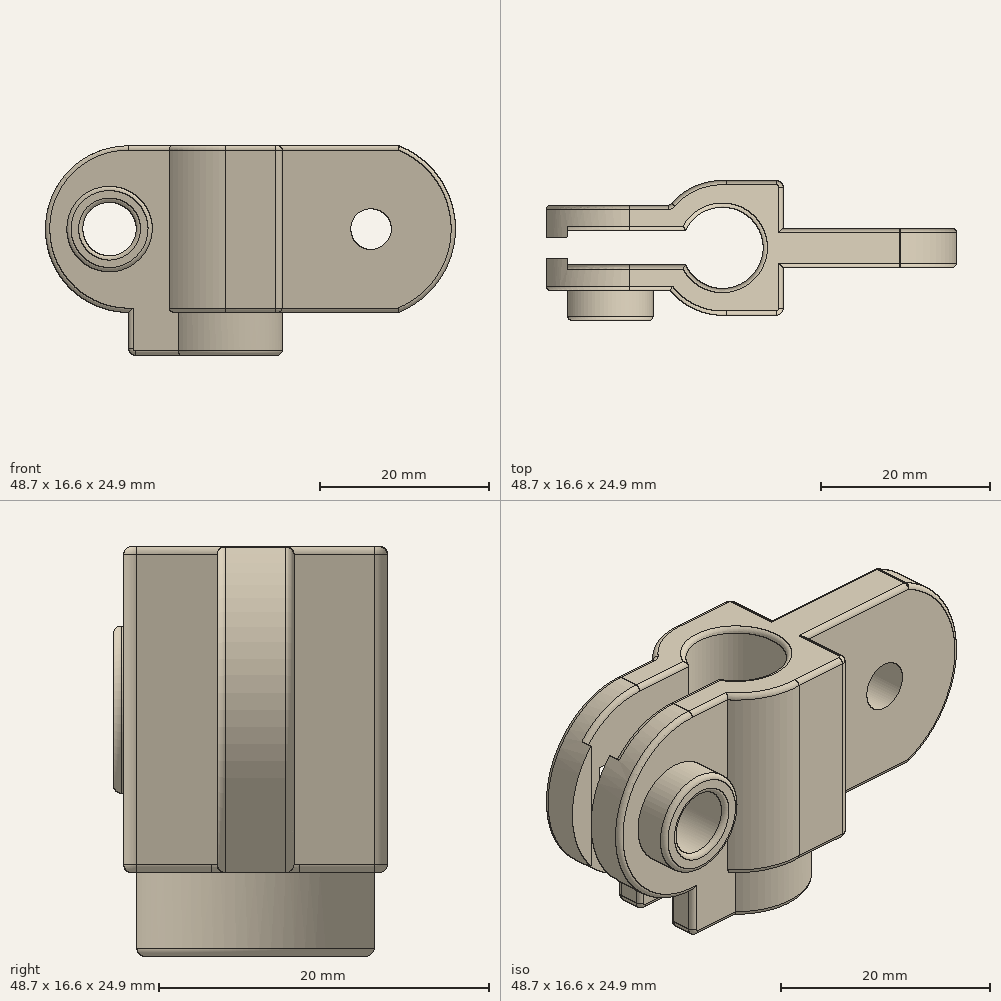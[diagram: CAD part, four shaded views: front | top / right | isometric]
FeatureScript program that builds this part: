
annotation { "Feature Type Name" : "Feature", "Feature Type Description" : "" }
export const myFeature = defineFeature(function(context is Context, id is Id, definition is map)
    precondition{}
    {
        {
            var Q0;
            Q0=qCreatedBy(makeId("Front.planeOp"),FACE);
            var sketch = newSketch(context, id + "F0", { "sketchPlane" : qUnion([Q0])});
            skLineSegment(sketch, "E0.bottom", {"start": v(4.6, 9.9) * mm, "end": v(-11.3, 9.9) * mm});
            skLineSegment(sketch, "E0.top", {"start": v(4.6, -9.9) * mm, "end": v(-11.3, -9.9) * mm});
            skLineSegment(sketch, "E0.right", {"start": v(-11.3, 9.9) * mm, "end": v(-11.3, -9.9) * mm});
            skPoint(sketch, "E0.middle", {"position": v(0, 0) * mm});
            skPoint(sketch, "E1.orphan", {"position": v(11.3, -9.9) * mm});
            skPoint(sketch, "E2.orphan", {"position": v(11.3, 9.9) * mm});
            skPoint(sketch, "E3.start.orphan", {"position": v(11.3, 0) * mm});
            skArc(sketch, "E4.trimOffspring", {"start": v(4.6, -9.9) * mm, "mid": v(11.3, 0) * mm, "end": v(4.6, 9.9) * mm});
            skLineSegment(sketch, "E5", {"start": v(11.3, 0) * mm, "end": v(3.68, 0) * mm});
            skLineSegment(sketch, "E6", {"start": v(-11.3, -9.9) * mm, "end": v(-9.3, -9.9) * mm});
            skLineSegment(sketch, "E7", {"start": v(-9.3, -9.9) * mm, "end": v(-9.3, 9.9) * mm});
            skPoint(sketch, "E8.endSnap0", {"position": v(-9.3, 0) * mm});
            skLineSegment(sketch, "E9", {"start": v(3.68, 0) * mm, "end": v(-1.14, 0) * mm});
            skCircle(sketch, "E10", {"center": v(1.27, 0) * mm, "radius": 2.41 * mm});
            skSolve(sketch);
        }
        {
            var Q0;
            Q0 = qSketchRegion(id + "F0", true);
            extrude(context, id + "F1", {"entities" : qUnion([Q0]), "depth" : 4.67 * mm});
        }
        {
            var Q0;
            Q0=makeQuery(id+"F1.opExtrude","SWEPT_FACE",FACE,{"disambiguationData":[OSD([sQuery(id+"F0.wireOp",EDGE,"E0.bottom")])]});
            var sketch = newSketch(context, id + "F2", { "sketchPlane" : qUnion([Q0])});
            skLineSegment(sketch, "E11", {"start": v(-11.3, -4.67) * mm, "end": v(-9.3, -4.67) * mm});
            skLineSegment(sketch, "E12", {"start": v(-9.3, -4.67) * mm, "end": v(-9.3, 0) * mm});
            skLineSegment(sketch, "E13", {"start": v(-9.3, 0) * mm, "end": v(-11.3, 0) * mm});
            skPoint(sketch, "E14.endSnap0", {"position": v(-11.3, -2.34) * mm});
            skLineSegment(sketch, "E15", {"start": v(-9.3, -2.34) * mm, "end": v(-9.3, -10.34) * mm});
            skLineSegment(sketch, "E16", {"start": v(-9.3, -9.55) * mm, "end": v(-9.3, 4.88) * mm});
            skLineSegment(sketch, "E17", {"start": v(-10.08, 5.66) * mm, "end": v(-17, 5.66) * mm});
            skLineSegment(sketch, "E18", {"start": v(-10.08, -10.34) * mm, "end": v(-17, -10.34) * mm});
            skLineSegment(sketch, "E19", {"start": v(-22.7, -7.42) * mm, "end": v(-27.19, -7.42) * mm});
            skLineSegment(sketch, "E20", {"start": v(-22.7, 2.74) * mm, "end": v(-26.33, 2.74) * mm});
            skArc(sketch, "E21", {"start": v(-16, 5.66) * mm, "mid": v(-19.7, 5.01) * mm, "end": v(-22.7, 2.74) * mm});
            skPoint(sketch, "E21.third.point", {"position": v(-16, 5.66) * mm});
            skPoint(sketch, "E22.orphan", {"position": v(-22.7, 5.66) * mm});
            skPoint(sketch, "E23.orphan", {"position": v(-22.7, -10.34) * mm});
            skArc(sketch, "E24.trimOffspring", {"start": v(-22.7, -7.42) * mm, "mid": v(-19.7, -9.69) * mm, "end": v(-16, -10.34) * mm});
            skArc(sketch, "E25", {"start": v(-20.88, -4.37) * mm, "mid": v(-11.68, -2.34) * mm, "end": v(-20.88, -0.3) * mm});
            skLineSegment(sketch, "E26", {"start": v(-22.7, -0.3) * mm, "end": v(-20.88, -0.3) * mm});
            skLineSegment(sketch, "E27", {"start": v(-22.7, -4.37) * mm, "end": v(-20.88, -4.37) * mm});
            skPoint(sketch, "E28.visualSharp", {"position": v(-9.3, -10.34) * mm});
            skArc(sketch, "E28.filletArc", {"start": v(-10.08, -10.34) * mm, "mid": v(-9.53, -10.1) * mm, "end": v(-9.3, -9.55) * mm});
            skPoint(sketch, "E29.visualSharp", {"position": v(-9.3, 5.66) * mm});
            skArc(sketch, "E29.filletArc", {"start": v(-9.3, 4.88) * mm, "mid": v(-9.53, 5.43) * mm, "end": v(-10.08, 5.66) * mm});
            skLineSegment(sketch, "E30", {"start": v(-20.88, -0.3) * mm, "end": v(-35.62, -0.3) * mm});
            skLineSegment(sketch, "E31", {"start": v(-35.62, 2.74) * mm, "end": v(-22.7, 2.74) * mm});
            skLineSegment(sketch, "E32", {"start": v(-22.7, -4.37) * mm, "end": v(-35.62, -4.37) * mm});
            skLineSegment(sketch, "E33", {"start": v(-35.62, -7.42) * mm, "end": v(-27.19, -7.42) * mm});
            skLineSegment(sketch, "E34", {"start": v(-22.7, 2.74) * mm, "end": v(-31.35, 2.74) * mm});
            skLineSegment(sketch, "E35", {"start": v(-22.7, 2.74) * mm, "end": v(-37.44, 2.74) * mm});
            skLineSegment(sketch, "E36", {"start": v(-35.62, -0.3) * mm, "end": v(-37.44, -0.3) * mm});
            skLineSegment(sketch, "E37", {"start": v(-37.44, -0.3) * mm, "end": v(-37.44, 2.74) * mm});
            skLineSegment(sketch, "E38", {"start": v(-37.44, -4.37) * mm, "end": v(-37.44, -7.42) * mm});
            skLineSegment(sketch, "E39", {"start": v(-37.44, -7.42) * mm, "end": v(-35.62, -7.42) * mm});
            skLineSegment(sketch, "E40", {"start": v(-35.62, -4.37) * mm, "end": v(-37.44, -4.37) * mm});
            skSolve(sketch);
        }
        {
            var Q0;
            Q0 = qSketchRegion(id + "F2", true);
            extrude(context, id + "F3", {"entities" : qUnion([Q0]), "operationType" : NewBodyOperationType.ADD, "oppositeDirection" : true, "depth" : 19.8 * mm});
        }
        {
            var Q0;
            Q0=makeQuery(id+"F3.opExtrude","CAP_EDGE",EDGE,{"disambiguationData":[OSD([sQuery(id+"F2.wireOp",EDGE,"E37")])],"isStart":true});
            var Q1;
            Q1=makeQuery(id+"F3.opExtrude","CAP_EDGE",EDGE,{"disambiguationData":[OSD([sQuery(id+"F2.wireOp",EDGE,"E38")])],"isStart":true});
            var Q2;
            Q2=makeQuery(id+"F3.opExtrude","CAP_EDGE",EDGE,{"disambiguationData":[OSD([sQuery(id+"F2.wireOp",EDGE,"E37")])],"isStart":false});
            var Q3;
            Q3=makeQuery(id+"F3.opExtrude","CAP_EDGE",EDGE,{"disambiguationData":[OSD([sQuery(id+"F2.wireOp",EDGE,"E38")])],"isStart":false});
            fillet(context, id + "F4", {"entities" : qUnion([Q0, Q1, Q2, Q3]), "radius" : 9.9 * mm, "tangentPropagation" : true, "allowEdgeOverflow" : false});
        }
        {
            var Q0;
            Q0=makeQuery(id+"F3.opExtrude","SWEPT_FACE",FACE,{"disambiguationData":[OSD([sQuery(id+"F2.wireOp",EDGE,"E35")])]});
            var sketch = newSketch(context, id + "F5", { "sketchPlane" : qUnion([Q0])});
            skPoint(sketch, "E41.endSnap0", {"position": v(35.62, 0) * mm});
            skLineSegment(sketch, "E42", {"start": v(26.64, 0) * mm, "end": v(22.7, 0) * mm});
            skLineSegment(sketch, "E43", {"start": v(33, 0) * mm, "end": v(37.44, 0) * mm});
            skLineSegment(sketch, "E44", {"start": v(29.82, 3.17) * mm, "end": v(26.64, 3.18) * mm});
            skLineSegment(sketch, "E45", {"start": v(26.64, 3.18) * mm, "end": v(26.64, -3.17) * mm});
            skLineSegment(sketch, "E46", {"start": v(26.64, -3.17) * mm, "end": v(33, -3.17) * mm});
            skLineSegment(sketch, "E47", {"start": v(33, -3.17) * mm, "end": v(33, 3.17) * mm});
            skLineSegment(sketch, "E48", {"start": v(33, 3.17) * mm, "end": v(29.82, 3.17) * mm});
            skSolve(sketch);
        }
        {
            var Q0;
            Q0 = qSketchRegion(id + "F5", true);
            extrude(context, id + "F6", {"entities" : qUnion([Q0]), "operationType" : NewBodyOperationType.REMOVE, "oppositeDirection" : true, "depth" : 5.08 * mm});
        }
        {
            var Q0;
            Q0=makeQuery(id+"F3.opExtrude","SWEPT_FACE",FACE,{"disambiguationData":[OSD([sQuery(id+"F2.wireOp",EDGE,"E27"),sQuery(id+"F2.wireOp",EDGE,"E32"),sQuery(id+"F2.wireOp",EDGE,"E40")])]});
            var sketch = newSketch(context, id + "F7", { "sketchPlane" : qUnion([Q0])});
            skLineSegment(sketch, "E49", {"start": v(26.64, 0) * mm, "end": v(22.7, 0) * mm});
            skLineSegment(sketch, "E50", {"start": v(33, 0) * mm, "end": v(37.44, 0) * mm});
            skCircle(sketch, "E51", {"center": v(29.82, 0) * mm, "radius": 3.18 * mm});
            skSolve(sketch);
        }
        {
            var Q0;
            Q0 = qSketchRegion(id + "F7", true);
            extrude(context, id + "F8", {"entities" : qUnion([Q0]), "operationType" : NewBodyOperationType.REMOVE, "oppositeDirection" : true, "depth" : 25.4 * mm});
        }
        {
            var Q0;
            Q0=makeQuery(id+"F3.boolean.opBoolean","MERGE",FACE,{"derivedFrom":[makeQuery(id+"F1.opExtrude","SWEPT_FACE",FACE,{"disambiguationData":[OSD([sQuery(id+"F0.wireOp",EDGE,"E0.top"),sQuery(id+"F0.wireOp",EDGE,"E6")])]}),makeQuery(id+"F3.opExtrude","CAP_FACE",FACE,{"disambiguationData":[OSD([sQuery(id+"F2.wireOp",EDGE,"E16"),sQuery(id+"F2.wireOp",EDGE,"E17"),sQuery(id+"F2.wireOp",EDGE,"E18"),sQuery(id+"F2.wireOp",EDGE,"E19"),sQuery(id+"F2.wireOp",EDGE,"E21"),sQuery(id+"F2.wireOp",EDGE,"E24.trimOffspring"),sQuery(id+"F2.wireOp",EDGE,"E25"),sQuery(id+"F2.wireOp",EDGE,"E27"),sQuery(id+"F2.wireOp",EDGE,"E28.filletArc"),sQuery(id+"F2.wireOp",EDGE,"E29.filletArc"),sQuery(id+"F2.wireOp",EDGE,"E30"),sQuery(id+"F2.wireOp",EDGE,"E32"),sQuery(id+"F2.wireOp",EDGE,"E33"),sQuery(id+"F2.wireOp",EDGE,"E35"),sQuery(id+"F2.wireOp",EDGE,"E36"),sQuery(id+"F2.wireOp",EDGE,"E37"),sQuery(id+"F2.wireOp",EDGE,"E38"),sQuery(id+"F2.wireOp",EDGE,"E39"),sQuery(id+"F2.wireOp",EDGE,"E40")])],"isStart":false})]});
            var sketch = newSketch(context, id + "F9", { "sketchPlane" : qUnion([Q0])});
            skArc(sketch, "E52", {"start": v(-20.88, 0.3) * mm, "mid": v(-11.68, 2.34) * mm, "end": v(-20.88, 4.37) * mm});
            skArc(sketch, "E53", {"start": v(-21.62, -2.74) * mm, "mid": v(-9.3, 2.34) * mm, "end": v(-21.62, 7.42) * mm});
            skLineSegment(sketch, "E54", {"start": v(-22.7, -2.74) * mm, "end": v(-21.62, -2.74) * mm});
            skLineSegment(sketch, "E55", {"start": v(-1.45, 7.42) * mm, "end": v(-1.45, 7.82) * mm});
            skLineSegment(sketch, "E56", {"start": v(-20.88, 4.37) * mm, "end": v(-27.53, 4.37) * mm});
            skLineSegment(sketch, "E57", {"start": v(-21.62, 7.42) * mm, "end": v(-27.53, 7.42) * mm});
            skLineSegment(sketch, "E58", {"start": v(-27.53, 7.42) * mm, "end": v(-27.53, 4.37) * mm});
            skLineSegment(sketch, "E59", {"start": v(-22.7, -2.74) * mm, "end": v(-27.53, -2.74) * mm});
            skLineSegment(sketch, "E60", {"start": v(-27.53, -2.74) * mm, "end": v(-27.53, 0.3) * mm});
            skLineSegment(sketch, "E61", {"start": v(-27.53, 0.3) * mm, "end": v(-20.88, 0.3) * mm});
            skSolve(sketch);
        }
        {
            var Q0;
            Q0 = qSketchRegion(id + "F9", true);
            extrude(context, id + "F10", {"entities" : qUnion([Q0]), "operationType" : NewBodyOperationType.ADD, "depth" : 5.08 * mm});
        }
        {
            var Q0;
            Q0=makeQuery(id+"F10.opExtrude","CAP_EDGE",EDGE,{"disambiguationData":[OSD([sQuery(id+"F9.wireOp",EDGE,"E58")])],"isStart":false});
            var Q1;
            Q1=makeQuery(id+"F10.opExtrude","CAP_EDGE",EDGE,{"disambiguationData":[OSD([sQuery(id+"F9.wireOp",EDGE,"E60")])],"isStart":false});
            fillet(context, id + "F11", {"entities" : qUnion([Q0, Q1]), "radius" : 0.79 * mm, "tangentPropagation" : true, "allowEdgeOverflow" : false});
        }
        {
            var Q0;
            Q0=makeQuery(id+"F3.opExtrude","CAP_EDGE",EDGE,{"disambiguationData":[OSD([sQuery(id+"F2.wireOp",EDGE,"E21")])],"isStart":false});
            var Q1;
            {var subQ0=sQuery(id+"F2.wireOp",EDGE,"E29.filletArc");var subQ1=sQuery(id+"F2.wireOp",EDGE,"E16");Q1=makeQuery(id+"F3.boolean.opBoolean","SPLIT",EDGE,{"disambiguationData":[TD([makeQuery(id+"F3.opExtrude","SWEPT_FACE",FACE,{"disambiguationData":[OSD([subQ0])]})])],"derivedFrom":makeQuery(id+"F3.opExtrude","CAP_EDGE",EDGE,{"disambiguationData":[OSD([subQ1])],"isStart":false})});}
            var Q2;
            Q2=makeQuery(id+"F1.opExtrude","CAP_EDGE",EDGE,{"disambiguationData":[OSD([sQuery(id+"F0.wireOp",EDGE,"E0.top"),sQuery(id+"F0.wireOp",EDGE,"E6")])],"isStart":true});
            var Q3;
            Q3=makeQuery(id+"F1.opExtrude","CAP_EDGE",EDGE,{"disambiguationData":[OSD([sQuery(id+"F0.wireOp",EDGE,"E0.top"),sQuery(id+"F0.wireOp",EDGE,"E6")])],"isStart":false});
            var Q4;
            Q4=makeQuery(id+"F1.opExtrude","CAP_EDGE",EDGE,{"disambiguationData":[OSD([sQuery(id+"F0.wireOp",EDGE,"E4.trimOffspring")])],"isStart":false});
            var Q5;
            Q5=makeQuery(id+"F1.opExtrude","CAP_EDGE",EDGE,{"disambiguationData":[OSD([sQuery(id+"F0.wireOp",EDGE,"E4.trimOffspring")])],"isStart":true});
            var Q6;
            {var subQ0=sQuery(id+"F2.wireOp",EDGE,"E28.filletArc");var subQ1=sQuery(id+"F2.wireOp",EDGE,"E16");Q6=makeQuery(id+"F3.boolean.opBoolean","SPLIT",EDGE,{"disambiguationData":[TD([makeQuery(id+"F3.opExtrude","SWEPT_FACE",FACE,{"disambiguationData":[OSD([subQ0])]})])],"derivedFrom":makeQuery(id+"F3.opExtrude","CAP_EDGE",EDGE,{"disambiguationData":[OSD([subQ1])],"isStart":false})});}
            var Q7;
            Q7=makeQuery(id+"F3.opExtrude","CAP_EDGE",EDGE,{"disambiguationData":[OSD([sQuery(id+"F2.wireOp",EDGE,"E24.trimOffspring")])],"isStart":false});
            var Q8;
            Q8=makeQuery(id+"F10.opExtrude","CAP_FACE",FACE,{"disambiguationData":[OSD([sQuery(id+"F9.wireOp",EDGE,"E52"),sQuery(id+"F9.wireOp",EDGE,"E53"),sQuery(id+"F9.wireOp",EDGE,"E54"),sQuery(id+"F9.wireOp",EDGE,"E56"),sQuery(id+"F9.wireOp",EDGE,"E57"),sQuery(id+"F9.wireOp",EDGE,"E58"),sQuery(id+"F9.wireOp",EDGE,"E59"),sQuery(id+"F9.wireOp",EDGE,"E60"),sQuery(id+"F9.wireOp",EDGE,"E61")])],"isStart":false});
            fillet(context, id + "F12", {"entities" : qUnion([Q0, Q1, Q2, Q3, Q4, Q5, Q6, Q7, Q8]), "radius" : 0.5 * mm, "tangentPropagation" : true, "allowEdgeOverflow" : false});
        }
        {
            var Q0;
            Q0=makeQuery(id+"F10.boolean.opBoolean","MERGE",FACE,{"derivedFrom":[makeQuery(id+"F3.opExtrude","SWEPT_FACE",FACE,{"disambiguationData":[OSD([sQuery(id+"F2.wireOp",EDGE,"E19"),sQuery(id+"F2.wireOp",EDGE,"E33"),sQuery(id+"F2.wireOp",EDGE,"E39")])]}),makeQuery(id+"F10.opExtrude","SWEPT_FACE",FACE,{"disambiguationData":[OSD([sQuery(id+"F9.wireOp",EDGE,"E57")])]})]});
            var sketch = newSketch(context, id + "F13", { "sketchPlane" : qUnion([Q0])});
            skCircle(sketch, "E62", {"center": v(-29.82, 0) * mm, "radius": 3.18 * mm});
            skLineSegment(sketch, "E63", {"start": v(-26.64, 0) * mm, "end": v(-24.74, 0) * mm});
            skCircle(sketch, "E64", {"center": v(-29.82, 0) * mm, "radius": 5.08 * mm});
            skLineSegment(sketch, "E65", {"start": v(-33, 0) * mm, "end": v(-34.9, 0) * mm});
            skSolve(sketch);
        }
        {
            var Q0;
            Q0 = qSketchRegion(id + "F13", true);
            extrude(context, id + "F14", {"entities" : qUnion([Q0]), "operationType" : NewBodyOperationType.ADD, "depth" : 3.56 * mm});
        }
        {
            var Q0;
            Q0=makeQuery(id+"F14.opExtrude","CAP_FACE",FACE,{"disambiguationData":[OSD([sQuery(id+"F13.wireOp",EDGE,"E62"),sQuery(id+"F13.wireOp",EDGE,"E64")])],"isStart":false});
            var Q1;
            Q1=makeQuery(id+"F10.boolean.opBoolean","MERGE",FACE,{"derivedFrom":[makeQuery(id+"F3.opExtrude","SWEPT_FACE",FACE,{"disambiguationData":[OSD([sQuery(id+"F2.wireOp",EDGE,"E35")])]}),makeQuery(id+"F10.opExtrude","SWEPT_FACE",FACE,{"disambiguationData":[OSD([sQuery(id+"F9.wireOp",EDGE,"E54"),sQuery(id+"F9.wireOp",EDGE,"E59")])]})]});
            fillet(context, id + "F15", {"entities" : qUnion([Q0, Q1]), "radius" : 0.5 * mm, "tangentPropagation" : true, "allowEdgeOverflow" : false});
        }
        {
            var Q0;
            Q0=makeQuery(id+"F10.boolean.opBoolean","MERGE",FACE,{"derivedFrom":[makeQuery(id+"F3.opExtrude","SWEPT_FACE",FACE,{"disambiguationData":[OSD([sQuery(id+"F2.wireOp",EDGE,"E30"),sQuery(id+"F2.wireOp",EDGE,"E36")])]}),makeQuery(id+"F10.opExtrude","SWEPT_FACE",FACE,{"disambiguationData":[OSD([sQuery(id+"F9.wireOp",EDGE,"E61")])]})]});
            var sketch = newSketch(context, id + "F16", { "sketchPlane" : qUnion([Q0])});
            skLineSegment(sketch, "E66", {"start": v(-34.9, -0.25) * mm, "end": v(-34.9, 6.63) * mm});
            skLineSegment(sketch, "E67", {"start": v(-34.9, -0.25) * mm, "end": v(-34.9, -6.63) * mm});
            skArc(sketch, "E68", {"start": v(-34.9, 6.63) * mm, "mid": v(-37.44, 0) * mm, "end": v(-34.9, -6.63) * mm});
            skPoint(sketch, "E69.start.orphan", {"position": v(-37.44, -0.25) * mm});
            skSolve(sketch);
        }
        {
            var Q0;
            Q0 = qSketchRegion(id + "F16", true);
            extrude(context, id + "F17", {"entities" : qUnion([Q0]), "operationType" : NewBodyOperationType.ADD, "depth" : 0.76 * mm});
        }
        {
            var Q0;
            Q0=makeQuery(id+"F10.boolean.opBoolean","MERGE",FACE,{"derivedFrom":[makeQuery(id+"F3.opExtrude","SWEPT_FACE",FACE,{"disambiguationData":[OSD([sQuery(id+"F2.wireOp",EDGE,"E27"),sQuery(id+"F2.wireOp",EDGE,"E32"),sQuery(id+"F2.wireOp",EDGE,"E40")])]}),makeQuery(id+"F10.opExtrude","SWEPT_FACE",FACE,{"disambiguationData":[OSD([sQuery(id+"F9.wireOp",EDGE,"E56")])]})]});
            var sketch = newSketch(context, id + "F18", { "sketchPlane" : qUnion([Q0])});
            skLineSegment(sketch, "E70", {"start": v(34.9, 6.62) * mm, "end": v(34.9, -6.62) * mm});
            skArc(sketch, "E71", {"start": v(34.9, -6.62) * mm, "mid": v(37.44, 0) * mm, "end": v(34.9, 6.62) * mm});
            skPoint(sketch, "E72.start.orphan", {"position": v(37.44, 0) * mm});
            skSolve(sketch);
        }
        {
            var Q0;
            Q0 = qSketchRegion(id + "F18", true);
            extrude(context, id + "F19", {"entities" : qUnion([Q0]), "operationType" : NewBodyOperationType.ADD, "depth" : 0.76 * mm});
        }
        {
            var Q0;
            Q0=makeQuery(id+"F3.boolean.opBoolean","MERGE",FACE,{"derivedFrom":[makeQuery(id+"F1.opExtrude","SWEPT_FACE",FACE,{"disambiguationData":[OSD([sQuery(id+"F0.wireOp",EDGE,"E0.bottom")])]}),makeQuery(id+"F3.opExtrude","CAP_FACE",FACE,{"disambiguationData":[OSD([sQuery(id+"F2.wireOp",EDGE,"E16"),sQuery(id+"F2.wireOp",EDGE,"E17"),sQuery(id+"F2.wireOp",EDGE,"E18"),sQuery(id+"F2.wireOp",EDGE,"E19"),sQuery(id+"F2.wireOp",EDGE,"E21"),sQuery(id+"F2.wireOp",EDGE,"E24.trimOffspring"),sQuery(id+"F2.wireOp",EDGE,"E25"),sQuery(id+"F2.wireOp",EDGE,"E27"),sQuery(id+"F2.wireOp",EDGE,"E28.filletArc"),sQuery(id+"F2.wireOp",EDGE,"E29.filletArc"),sQuery(id+"F2.wireOp",EDGE,"E30"),sQuery(id+"F2.wireOp",EDGE,"E32"),sQuery(id+"F2.wireOp",EDGE,"E33"),sQuery(id+"F2.wireOp",EDGE,"E35"),sQuery(id+"F2.wireOp",EDGE,"E36"),sQuery(id+"F2.wireOp",EDGE,"E37"),sQuery(id+"F2.wireOp",EDGE,"E38"),sQuery(id+"F2.wireOp",EDGE,"E39"),sQuery(id+"F2.wireOp",EDGE,"E40")])],"isStart":true})]});
            fillet(context, id + "F20", {"entities" : qUnion([Q0]), "radius" : 0.5 * mm, "tangentPropagation" : true, "allowEdgeOverflow" : false});
        }
    });
